FCSTD DOCUMENT  (FreeCAD 1.0R39109 (Git))
Label: 10_drawer_96mm_assembly
License: All rights reserved
LicenseURL: http://en.wikipedia.org/wiki/All_rights_reserved
objects: App::FeaturePython×17, App::Link×6, Assembly::JointGroup×1, Assembly::AssemblyObject×1
EXTERNAL_REF file=60_drawer_all_bottom.FCStd obj=Body
EXTERNAL_REF file=15_drawer_96mm_long.FCStd obj=Body
EXTERNAL_REF file=16_drawer_96mm_short.FCStd obj=Body
EXTERNAL_REF file=17_drawer_96mm_front.FCStd obj=Body

FEATURE [App::Link] Body
  LinkedObject = -> <external 60_drawer_all_bottom.FCStd>#Body
FEATURE [App::FeaturePython] GroundedJoint  # Assembly grounded joint (typed FeaturePython)
  ObjectToGround = -> Body
FEATURE [App::Link] Body001
  LinkPlacement = pos=(-0.0692255,177.5,34.4999) rot=(0.999999,-0.001116,0.001116;1.5708rad)
  LinkedObject = -> <external 15_drawer_96mm_long.FCStd>#Body
  Placement = pos=(-0.0692255,177.5,34.4999) rot=(0.999999,-0.001116,0.001116;1.5708rad)
FEATURE [App::Link] Body002
  LinkPlacement = pos=(2.3e-15,-177.5,34) rot=(0,0.707107,0.707107;3.14159rad)
  LinkedObject = -> <external 15_drawer_96mm_long.FCStd>#Body
  Placement = pos=(2.3e-15,-177.5,34) rot=(0,0.707107,0.707107;3.14159rad)
FEATURE [App::Link] Body003
  LinkPlacement = pos=(-231.5,-4.06e-14,34) rot=(0.57735,0.57735,0.57735;2.0944rad)
  LinkedObject = -> <external 16_drawer_96mm_short.FCStd>#Body
  Placement = pos=(-231.5,-4.06e-14,34) rot=(0.57735,0.57735,0.57735;2.0944rad)
FEATURE [App::Link] Body004
  LinkPlacement = pos=(231.5,-6.4e-15,34) rot=(0.57735,-0.57735,-0.57735;2.0944rad)
  LinkedObject = -> <external 16_drawer_96mm_short.FCStd>#Body
  Placement = pos=(231.5,-6.4e-15,34) rot=(0.57735,-0.57735,-0.57735;2.0944rad)
FEATURE [App::FeaturePython] Joint  label="Back1"  # Assembly joint (typed FeaturePython)
  Activated = true
  AngleMax = 0
  AngleMin = 0
  Detach1 = false
  Detach2 = false
  Distance = 0
  Distance2 = 0
  EnableAngleMax = false
  EnableAngleMin = false
  EnableLengthMax = false
  EnableLengthMin = false
  JointType = 5 (Distance)
  LengthMax = 0
  LengthMin = 0
  Placement1 = pos=(-2.3e-15,168.5,3.25) rot=(-1,0,0;1.5708rad)
  Placement2 = pos=(6.54e-14,-30.75,9) rot=(0.707107,0.707107,0;3.14159rad)
  Reference1 = -> Assembly [Body.Face1,Body.Face1]
  Reference2 = -> Assembly [Body001.Face7,Body001.Face7]
FEATURE [App::FeaturePython] Joint001  label="Back2"  # Assembly joint (typed FeaturePython)
  Activated = true
  AngleMax = 0
  AngleMin = 0
  Detach1 = false
  Detach2 = false
  Distance = 0.5
  Distance2 = 0
  EnableAngleMax = false
  EnableAngleMin = false
  EnableLengthMax = false
  EnableLengthMin = false
  JointType = 5 (Distance)
  LengthMax = 0
  LengthMin = 0
  Placement1 = pos=(7.41e-14,-34,12) rot=(0.57735,0.57735,-0.57735;2.0944rad)
  Placement2 = pos=(-2e-16,4.1e-15,0) rot=(0,0,1;0rad)
  Reference1 = -> Assembly [Body001.Face8,Body001.Vertex9]
  Reference2 = -> Assembly [Body.Face5,Body.Vertex1]
FEATURE [App::FeaturePython] Joint002  label="Back3"  # Assembly joint (typed FeaturePython)
  Activated = true
  AngleMax = 0
  AngleMin = 0
  Detach1 = false
  Detach2 = false
  Distance = 6
  Distance2 = 0
  EnableAngleMax = false
  EnableAngleMin = false
  EnableLengthMax = false
  EnableLengthMin = false
  JointType = 5 (Distance)
  LengthMax = 0
  LengthMin = 0
  Placement1 = pos=(-216.5,1.03295,7.34884) rot=(-0.57735,-0.57735,0.57735;2.0944rad)
  Placement2 = pos=(-222.5,-5.2e-15,3.25) rot=(-0.57735,-0.57735,0.57735;2.0944rad)
  Reference1 = -> Assembly [Body001.Face2,Body001.Face2]
  Reference2 = -> Assembly [Body.Face4,Body.Face4]
FEATURE [App::FeaturePython] Joint003  label="Left1"  # Assembly joint (typed FeaturePython)
  Activated = true
  AngleMax = 0
  AngleMin = 0
  Detach1 = false
  Detach2 = false
  Distance = 0
  Distance2 = 0
  EnableAngleMax = false
  EnableAngleMin = false
  EnableLengthMax = false
  EnableLengthMin = false
  JointType = 5 (Distance)
  LengthMax = 0
  LengthMin = 0
  Placement1 = pos=(-2e-16,4.1e-15,6.5) rot=(0,0,1;0rad)
  Placement2 = pos=(2.8e-15,-27.5,12) rot=(-0.57735,-0.57735,-0.57735;2.0944rad)
  Reference1 = -> Assembly [Body.Face6,Body.Face6]
  Reference2 = -> Assembly [Body003.Face6,Body003.Face6]
FEATURE [App::FeaturePython] Joint004  label="Left2"  # Assembly joint (typed FeaturePython)
  Activated = true
  AngleMax = 0
  AngleMin = 0
  Detach1 = false
  Detach2 = false
  Distance = 0
  Distance2 = 0
  EnableAngleMax = false
  EnableAngleMin = false
  EnableLengthMax = false
  EnableLengthMin = false
  JointType = 5 (Distance)
  LengthMax = 0
  LengthMin = 0
  Placement1 = pos=(9.3e-15,-30.75,9) rot=(-0.707107,-0.707107,0;3.14159rad)
  Placement2 = pos=(-222.5,-5.2e-15,3.25) rot=(-0.57735,-0.57735,0.57735;2.0944rad)
  Reference1 = -> Assembly [Body003.Face7,Body003.Face7]
  Reference2 = -> Assembly [Body.Face4,Body.Face4]
FEATURE [App::FeaturePython] Joint005  label="Left3"  # Assembly joint (typed FeaturePython)
  Activated = true
  AngleMax = 0
  AngleMin = 0
  Detach1 = false
  Detach2 = false
  Distance = 9
  Distance2 = 0
  EnableAngleMax = false
  EnableAngleMin = false
  EnableLengthMax = false
  EnableLengthMin = false
  JointType = 5 (Distance)
  LengthMax = 0
  LengthMin = 0
  Placement1 = pos=(2.3e-15,-168.5,3.25) rot=(0,-0.707107,0.707107;3.14159rad)
  Placement2 = pos=(-177.5,1.03295,7.34884) rot=(-0.57735,-0.57735,0.57735;2.0944rad)
  Reference1 = -> Assembly [Body.Face3,Body.Face3]
  Reference2 = -> Assembly [Body003.Face2,Body003.Face2]
FEATURE [App::FeaturePython] Joint006  label="Distance"  # Assembly joint (typed FeaturePython)
  Activated = true
  AngleMax = 0
  AngleMin = 0
  Detach1 = false
  Detach2 = false
  Distance = 0
  Distance2 = 0
  EnableAngleMax = false
  EnableAngleMin = false
  EnableLengthMax = false
  EnableLengthMin = false
  JointType = 5 (Distance)
  LengthMax = 0
  LengthMin = 0
  Placement1 = pos=(6.6e-14,-27.5,12) rot=(-0.57735,-0.57735,-0.57735;2.0944rad)
  Placement2 = pos=(-2e-16,4.1e-15,6.5) rot=(0,0,1;0rad)
  Reference1 = -> Assembly [Body002.Face6,Body002.Face6]
  Reference2 = -> Assembly [Body.Face6,Body.Face6]
FEATURE [App::FeaturePython] Joint007  label="Distance001"  # Assembly joint (typed FeaturePython)
  Activated = true
  AngleMax = 0
  AngleMin = 0
  Detach1 = false
  Detach2 = false
  Distance = 0
  Distance2 = 0
  EnableAngleMax = false
  EnableAngleMin = false
  EnableLengthMax = false
  EnableLengthMin = false
  JointType = 5 (Distance)
  LengthMax = 0
  LengthMin = 0
  Placement1 = pos=(2.3e-15,-168.5,3.25) rot=(0,-0.707107,0.707107;3.14159rad)
  Placement2 = pos=(6.88e-14,-30.75,9) rot=(0.707107,0.707107,0;3.14159rad)
  Reference1 = -> Assembly [Body.Face3,Body.Face3]
  Reference2 = -> Assembly [Body002.Face7,Body002.Vertex8]
FEATURE [App::FeaturePython] Joint008  label="Distance002"  # Assembly joint (typed FeaturePython)
  Activated = true
  AngleMax = 0
  AngleMin = 0
  Detach1 = false
  Detach2 = false
  Distance = -6
  Distance2 = 0
  EnableAngleMax = false
  EnableAngleMin = false
  EnableLengthMax = false
  EnableLengthMin = false
  JointType = 5 (Distance)
  LengthMax = 0
  LengthMin = 0
  Placement1 = pos=(222.5,5.2e-15,3.25) rot=(0.57735,-0.57735,0.57735;4.18879rad)
  Placement2 = pos=(-216.5,1.03295,7.34884) rot=(-0.57735,-0.57735,0.57735;2.0944rad)
  Reference1 = -> Assembly [Body.Face2,Body.Face2]
  Reference2 = -> Assembly [Body002.Face2,Body002.Face2]
FEATURE [App::FeaturePython] Joint009  label="Rigth1"  # Assembly joint (typed FeaturePython)
  Activated = true
  AngleMax = 0
  AngleMin = 0
  Detach1 = false
  Detach2 = false
  Distance = 0
  Distance2 = 0
  EnableAngleMax = false
  EnableAngleMin = false
  EnableLengthMax = false
  EnableLengthMin = false
  JointType = 5 (Distance)
  LengthMax = 0
  LengthMin = 0
  Placement1 = pos=(-1.05e-14,-27.5,12) rot=(0.57735,0.57735,0.57735;4.18879rad)
  Placement2 = pos=(-2e-16,4.1e-15,6.5) rot=(0,0,1;0rad)
  Reference1 = -> Assembly [Body004.Face6,Body004.Face6]
  Reference2 = -> Assembly [Body.Face6,Body.Face6]
FEATURE [App::FeaturePython] Joint010  label="Rigth2"  # Assembly joint (typed FeaturePython)
  Activated = true
  AngleMax = 0
  AngleMin = 0
  Detach1 = false
  Detach2 = false
  Distance = 0
  Distance2 = 0
  EnableAngleMax = false
  EnableAngleMin = false
  EnableLengthMax = false
  EnableLengthMin = false
  JointType = 5 (Distance)
  LengthMax = 0
  LengthMin = 0
  Placement1 = pos=(-4.9e-15,-30.75,9) rot=(0.707107,0.707107,0;3.14159rad)
  Placement2 = pos=(222.5,5.2e-15,3.25) rot=(0.57735,-0.57735,0.57735;4.18879rad)
  Reference1 = -> Assembly [Body004.Face7,Body004.Vertex8]
  Reference2 = -> Assembly [Body.Face2,Body.Vertex5]
FEATURE [App::FeaturePython] Joint011  label="Right3"  # Assembly joint (typed FeaturePython)
  Activated = true
  AngleMax = 0
  AngleMin = 0
  Detach1 = false
  Detach2 = false
  Distance = 9
  Distance2 = 0
  EnableAngleMax = false
  EnableAngleMin = false
  EnableLengthMax = false
  EnableLengthMin = false
  JointType = 5 (Distance)
  LengthMax = 0
  LengthMin = 0
  Placement1 = pos=(2.3e-15,-168.5,3.25) rot=(0,-0.707107,0.707107;3.14159rad)
  Placement2 = pos=(177.5,1.03295,7.34884) rot=(0.57735,-0.57735,0.57735;4.18879rad)
  Reference1 = -> Assembly [Body.Face3,Body.Vertex5]
  Reference2 = -> Assembly [Body004.Face3,Body004.Face3]
FEATURE [App::Link] Body005
  LinkPlacement = pos=(2.5e-15,-177.5,33.5) rot=(0,-0.707107,0.707107;3.14159rad)
  LinkedObject = -> <external 17_drawer_96mm_front.FCStd>#Body
  Placement = pos=(2.5e-15,-177.5,33.5) rot=(0,-0.707107,0.707107;3.14159rad)
FEATURE [App::FeaturePython] Joint012  label="Front1"  # Assembly joint (typed FeaturePython)
  Activated = true
  AngleMax = 0
  AngleMin = 0
  Detach1 = false
  Detach2 = false
  Distance = 0
  Distance2 = 0
  EnableAngleMax = false
  EnableAngleMin = false
  EnableLengthMax = false
  EnableLengthMin = false
  JointType = 5 (Distance)
  LengthMax = 0
  LengthMin = 0
  Placement1 = pos=(2e-15,0,0) rot=(0,0,1;0rad)
  Placement2 = pos=(3e-15,0,0) rot=(0,0,1;0rad)
  Reference1 = -> Assembly [Body005.Face5,Body005.Face5]
  Reference2 = -> Assembly [Body002.Face4,Body002.Face4]
FEATURE [App::FeaturePython] Joint013  label="Front2"  # Assembly joint (typed FeaturePython)
  Activated = true
  AngleMax = 0
  AngleMin = 0
  Detach1 = false
  Detach2 = false
  Distance = 6
  Distance2 = 0
  EnableAngleMax = false
  EnableAngleMin = false
  EnableLengthMax = false
  EnableLengthMin = false
  JointType = 5 (Distance)
  LengthMax = 0
  LengthMin = 0
  Placement1 = pos=(8.3e-15,40,7.5) rot=(-1,0,0;1.5708rad)
  Placement2 = pos=(7.1e-15,-46.5,7.5) rot=(0,0.707107,-0.707107;3.14159rad)
  Reference1 = -> Assembly [Body002.Face1,Body002.Face1]
  Reference2 = -> Assembly [Body005.Face3,Body005.Face3]
FEATURE [App::FeaturePython] Joint014  label="Distance003"  # Assembly joint (typed FeaturePython)
  Activated = true
  AngleMax = 0
  AngleMin = 0
  Detach1 = false
  Detach2 = false
  Distance = -29
  Distance2 = 0
  EnableAngleMax = false
  EnableAngleMin = false
  EnableLengthMax = false
  EnableLengthMin = false
  JointType = 5 (Distance)
  LengthMax = 0
  LengthMin = 0
  Placement1 = pos=(1.4e-15,0,0) rot=(0,0,1;0rad)
  Placement2 = pos=(260.5,0,7.5) rot=(-0.57735,0.57735,-0.57735;2.0944rad)
  Reference1 = -> Assembly [Body003.Face4,Body003.Face4]
  Reference2 = -> Assembly [Body005.Face2,Body005.Face2]
FEATURE [App::FeaturePython] Joint015  label="Distance004"  # Assembly joint (typed FeaturePython)
  Activated = true
  AngleMax = 0
  AngleMin = 0
  Detach1 = false
  Detach2 = false
  Distance = 0
  Distance2 = 0
  EnableAngleMax = false
  EnableAngleMin = false
  EnableLengthMax = false
  EnableLengthMin = false
  JointType = 5 (Distance)
  LengthMax = 0
  LengthMin = 0
  Placement1 = pos=(1.72e-14,40,7.5) rot=(-1,0,0;1.5708rad)
  Placement2 = pos=(6.2e-15,40,7.5) rot=(-1,0,0;1.5708rad)
  Reference1 = -> Assembly [Body001.Face1,Body001.Vertex2]
  Reference2 = -> Assembly [Body003.Face1,Body003.Vertex4]
FEATURE [Assembly::JointGroup] Joints
  Group = -> [GroundedJoint,Joint,Joint001,Joint002,Joint003,Joint004,Joint005,Joint006,Joint007,Joint008,Joint009,Joint010,Joint011,Joint012,Joint013,Joint014,Joint015]
FEATURE [Assembly::AssemblyObject] Assembly
  Group = -> [Joints,Body,GroundedJoint,Body001,Body002,Body003,Body004,Joint,Joint001,Joint002,Joint003,Joint004,Joint005,Joint006,Joint007,Joint008,Joint009,Joint010,Joint011,Body005,Joint012,Joint013,Joint014,Joint015]
  Origin = -> Origin
  Type = Assembly

RESOLVED EXTERNAL PARTS (link-assembly join: the EXTERNAL_REF files above that resolve inside this repo's crawl, each included once):
---- part 15_drawer_96mm_long.FCStd = doc fcstd_027bf1619f1c ----
FCSTD DOCUMENT  (FreeCAD 1.0R39109 (Git))
Label: 15_drawer_96mm_long
License: All rights reserved
LicenseURL: http://en.wikipedia.org/wiki/All_rights_reserved
objects: Sketcher::SketchObject×2, Spreadsheet::Sheet×1, PartDesign::Pad×1, PartDesign::Pocket×1, PartDesign::Body×1
note: 11 computed .brp shape members not serialized (recipe doc carries the construction recipe); baked Part::Feature solids carry a one-line shape summary decoded from their .brp

FEATURE [Spreadsheet::Sheet] Spreadsheet
  cells = A2='length; B2(length)=433; D2='space: 2mm; A3='width; B3(width)=80; D3='space: 2mm; A4='height; B4(height)=15; A6='Groove Depth; B6(grooveDepth)=6; A7='Groove Distance; B7(grooveDistance)=6; A8='Groove Width; B8(grooveWidth)=6.5
FEATURE [Sketcher::SketchObject] Sketch
  ArcFitTolerance = 0
  AttachmentSupport = -> [XY_Plane]
  FullyConstrained = true
  MakeInternals = false
  MapMode = 5
  expr: Constraints[11] = Spreadsheet.length
  expr: Constraints[12] = Spreadsheet.width
  sketch-geometry (5):
    g0: LineSegment StartX=-216.5 StartY=40 StartZ=0 EndX=216.5 EndY=40 EndZ=0
    g1: LineSegment StartX=216.5 StartY=40 StartZ=0 EndX=216.5 EndY=-40 EndZ=0
    g2: LineSegment StartX=216.5 StartY=-40 StartZ=0 EndX=-216.5 EndY=-40 EndZ=0
    g3: LineSegment StartX=-216.5 StartY=-40 StartZ=0 EndX=-216.5 EndY=40 EndZ=0
    g4: LineSegment [constr] StartX=-216.5 StartY=40 StartZ=0 EndX=216.5 EndY=-40 EndZ=0
  constraints (13):
    c: Coincident(g0,g1)
    c: Coincident(g1,g2)
    c: Coincident(g2,g3)
    c: Coincident(g3,g0)
    c: Horizontal(g0)
    c: Horizontal(g2)
    c: Vertical(g1)
    c: Vertical(g3)
    c: Coincident(g4,g1)
    c: Coincident(g0,g4)
    c: Symmetric(g0,g1,g-1)
    c: Distance(g0,g0) = 433
    c: Distance(g0,g2) = 80
FEATURE [PartDesign::Pad] Pad
  Direction = (0,0,1)
  Length = 15
  Length2 = 10
  Profile = -> Sketch
  ReferenceAxis = -> Sketch [N_Axis]
  Suppressed = false
  Type = 0
  expr: Length = Spreadsheet.height
FEATURE [Sketcher::SketchObject] Sketch001
  ArcFitTolerance = 1e-06
  AttachmentSupport = -> [YZ_Plane]
  ExternalGeometry = -> [Pad]
  FullyConstrained = true
  MakeInternals = false
  MapMode = 5
  Placement = pos=(0,0,0) rot=(0.57735,0.57735,0.57735;2.0944rad)
  sketch-geometry (4):
    g0: LineSegment StartX=-34 StartY=15 StartZ=0 EndX=-34 EndY=9 EndZ=0
    g1: LineSegment StartX=-34 StartY=9 StartZ=0 EndX=-27.5 EndY=9 EndZ=0
    g2: LineSegment StartX=-27.5 StartY=9 StartZ=0 EndX=-27.5 EndY=15 EndZ=0
    g3: LineSegment StartX=-27.5 StartY=15 StartZ=0 EndX=-34 EndY=15 EndZ=0
  constraints (12):
    c: Coincident(g0,g1)
    c: Coincident(g1,g2)
    c: Coincident(g2,g3)
    c: Coincident(g3,g0)
    c: Vertical(g0)
    c: Vertical(g2)
    c: Horizontal(g1)
    c: Horizontal(g3)
    c: PointOnObject(g0,g-3)
    c: DistanceX(g3,g3) = 6.5
    c: Distance(g-4,g0) = 6
    c: DistanceY(g2,g2) = 6
FEATURE [PartDesign::Pocket] Pocket
  BaseFeature = -> Pad
  Direction = (-1,0,0)
  Length = 5
  Length2 = 5
  Midplane = true
  Profile = -> Sketch001
  ReferenceAxis = -> Sketch001 [N_Axis]
  Suppressed = false
  Type = 1
FEATURE [PartDesign::Body] Body
  AllowCompound = false
  Group = -> [Sketch,Pad,Sketch001,Pocket]
  Origin = -> Origin
  Tip = -> Pocket
---- part 16_drawer_96mm_short.FCStd = doc fcstd_3ad6f7a57b24 ----
FCSTD DOCUMENT  (FreeCAD 1.0R39109 (Git))
Label: 16_drawer_96mm_short
License: All rights reserved
LicenseURL: http://en.wikipedia.org/wiki/All_rights_reserved
objects: Sketcher::SketchObject×2, Spreadsheet::Sheet×1, PartDesign::Pad×1, PartDesign::Pocket×1, PartDesign::Body×1
note: 11 computed .brp shape members not serialized (recipe doc carries the construction recipe); baked Part::Feature solids carry a one-line shape summary decoded from their .brp

FEATURE [Spreadsheet::Sheet] Spreadsheet
  cells = A2='length; B2(length)=355; D2='space: 1mm; A3='width; B3(width)=80; D3='space: 1mm; A4='height; B4(height)=15; A6='Groove Depth; B6(grooveDepth)=6; A7='Groove Distance; B7(grooveDistance)=6; A8='Groove Width; B8(grooveWidth)=6.5
FEATURE [Sketcher::SketchObject] Sketch
  ArcFitTolerance = 0
  AttachmentSupport = -> [XY_Plane]
  FullyConstrained = true
  MakeInternals = false
  MapMode = 5
  expr: Constraints[11] = Spreadsheet.length
  expr: Constraints[12] = Spreadsheet.width
  sketch-geometry (5):
    g0: LineSegment StartX=-177.5 StartY=40 StartZ=0 EndX=177.5 EndY=40 EndZ=0
    g1: LineSegment StartX=177.5 StartY=40 StartZ=0 EndX=177.5 EndY=-40 EndZ=0
    g2: LineSegment StartX=177.5 StartY=-40 StartZ=0 EndX=-177.5 EndY=-40 EndZ=0
    g3: LineSegment StartX=-177.5 StartY=-40 StartZ=0 EndX=-177.5 EndY=40 EndZ=0
    g4: LineSegment [constr] StartX=-177.5 StartY=40 StartZ=0 EndX=177.5 EndY=-40 EndZ=0
  constraints (13):
    c: Coincident(g0,g1)
    c: Coincident(g1,g2)
    c: Coincident(g2,g3)
    c: Coincident(g3,g0)
    c: Horizontal(g0)
    c: Horizontal(g2)
    c: Vertical(g1)
    c: Vertical(g3)
    c: Coincident(g4,g1)
    c: Coincident(g0,g4)
    c: Symmetric(g0,g1,g-1)
    c: Distance(g0,g0) = 355
    c: Distance(g0,g2) = 80
FEATURE [PartDesign::Pad] Pad
  Direction = (0,0,1)
  Length = 15
  Length2 = 10
  Profile = -> Sketch
  ReferenceAxis = -> Sketch [N_Axis]
  Suppressed = false
  Type = 0
  expr: Length = Spreadsheet.height
FEATURE [Sketcher::SketchObject] Sketch001
  ArcFitTolerance = 1e-06
  AttachmentSupport = -> [YZ_Plane]
  ExternalGeometry = -> [Pad]
  FullyConstrained = true
  MakeInternals = false
  MapMode = 5
  Placement = pos=(0,0,0) rot=(0.57735,0.57735,0.57735;2.0944rad)
  sketch-geometry (4):
    g0: LineSegment StartX=-34 StartY=15 StartZ=0 EndX=-34 EndY=9 EndZ=0
    g1: LineSegment StartX=-34 StartY=9 StartZ=0 EndX=-27.5 EndY=9 EndZ=0
    g2: LineSegment StartX=-27.5 StartY=9 StartZ=0 EndX=-27.5 EndY=15 EndZ=0
    g3: LineSegment StartX=-27.5 StartY=15 StartZ=0 EndX=-34 EndY=15 EndZ=0
  constraints (12):
    c: Coincident(g0,g1)
    c: Coincident(g1,g2)
    c: Coincident(g2,g3)
    c: Coincident(g3,g0)
    c: Vertical(g0)
    c: Vertical(g2)
    c: Horizontal(g1)
    c: Horizontal(g3)
    c: PointOnObject(g0,g-4)
    c: DistanceX(g3,g3) = 6.5
    c: Distance(g0,g0) = 6
    c: Distance(g-4,g0) = 6
FEATURE [PartDesign::Pocket] Pocket
  BaseFeature = -> Pad
  Direction = (-1,0,0)
  Length = 5
  Length2 = 5
  Midplane = true
  Profile = -> Sketch001
  ReferenceAxis = -> Sketch001 [N_Axis]
  Suppressed = false
  Type = 1
FEATURE [PartDesign::Body] Body
  AllowCompound = false
  Group = -> [Sketch,Pad,Sketch001,Pocket]
  Origin = -> Origin
  Tip = -> Pocket
---- part 17_drawer_96mm_front.FCStd = doc fcstd_0fb94227f05c ----
FCSTD DOCUMENT  (FreeCAD 1.0R39109 (Git))
Label: 17_drawer_96mm_front
License: All rights reserved
LicenseURL: http://en.wikipedia.org/wiki/All_rights_reserved
objects: Spreadsheet::Sheet×1, Sketcher::SketchObject×1, PartDesign::Pad×1, PartDesign::Body×1
note: 6 computed .brp shape members not serialized (recipe doc carries the construction recipe); baked Part::Feature solids carry a one-line shape summary decoded from their .brp

FEATURE [Spreadsheet::Sheet] Spreadsheet
  cells = A2='length; B2(length)=521; A3='width; B3(width)=93; A4='height; B4(height)=15; D9=433; D10==D9 + 30; E10==B2 - D10; E11==E10 / 2
FEATURE [Sketcher::SketchObject] Sketch
  ArcFitTolerance = 0
  AttachmentSupport = -> [XY_Plane]
  FullyConstrained = true
  MakeInternals = false
  MapMode = 5
  expr: Constraints[11] = Spreadsheet.length
  expr: Constraints[12] = Spreadsheet.width
  sketch-geometry (5):
    g0: LineSegment StartX=-260.5 StartY=46.5 StartZ=0 EndX=260.5 EndY=46.5 EndZ=0
    g1: LineSegment StartX=260.5 StartY=46.5 StartZ=0 EndX=260.5 EndY=-46.5 EndZ=0
    g2: LineSegment StartX=260.5 StartY=-46.5 StartZ=0 EndX=-260.5 EndY=-46.5 EndZ=0
    g3: LineSegment StartX=-260.5 StartY=-46.5 StartZ=0 EndX=-260.5 EndY=46.5 EndZ=0
    g4: LineSegment [constr] StartX=-260.5 StartY=46.5 StartZ=0 EndX=260.5 EndY=-46.5 EndZ=0
  constraints (13):
    c: Coincident(g0,g1)
    c: Coincident(g1,g2)
    c: Coincident(g2,g3)
    c: Coincident(g3,g0)
    c: Horizontal(g0)
    c: Horizontal(g2)
    c: Vertical(g1)
    c: Vertical(g3)
    c: Coincident(g4,g1)
    c: Coincident(g0,g4)
    c: Symmetric(g0,g1,g-1)
    c: Distance(g0,g0) = 521
    c: Distance(g0,g2) = 93
FEATURE [PartDesign::Pad] Pad
  Direction = (0,0,1)
  Length = 15
  Length2 = 10
  Profile = -> Sketch
  ReferenceAxis = -> Sketch [N_Axis]
  Suppressed = false
  Type = 0
  expr: Length = Spreadsheet.height
FEATURE [PartDesign::Body] Body
  AllowCompound = false
  Group = -> [Sketch,Pad]
  Origin = -> Origin
  Tip = -> Pad
---- part 60_drawer_all_bottom.FCStd = doc fcstd_0f60ed07a972 ----
FCSTD DOCUMENT  (FreeCAD 1.0R39109 (Git))
Label: 60_drawer_all_bottom
License: All rights reserved
LicenseURL: http://en.wikipedia.org/wiki/All_rights_reserved
objects: Spreadsheet::Sheet×1, Sketcher::SketchObject×1, PartDesign::Pad×1, PartDesign::Body×1
note: 6 computed .brp shape members not serialized (recipe doc carries the construction recipe); baked Part::Feature solids carry a one-line shape summary decoded from their .brp

FEATURE [Spreadsheet::Sheet] Spreadsheet
  cells = A2='length; B2(length)=445; A3='width; B3(width)=337; A4='height; B4(height)=6.5
FEATURE [Sketcher::SketchObject] Sketch
  ArcFitTolerance = 0
  AttachmentSupport = -> [XY_Plane]
  FullyConstrained = true
  MakeInternals = false
  MapMode = 5
  expr: Constraints[11] = Spreadsheet.length
  expr: Constraints[12] = Spreadsheet.width
  sketch-geometry (5):
    g0: LineSegment StartX=-222.5 StartY=168.5 StartZ=0 EndX=222.5 EndY=168.5 EndZ=0
    g1: LineSegment StartX=222.5 StartY=168.5 StartZ=0 EndX=222.5 EndY=-168.5 EndZ=0
    g2: LineSegment StartX=222.5 StartY=-168.5 StartZ=0 EndX=-222.5 EndY=-168.5 EndZ=0
    g3: LineSegment StartX=-222.5 StartY=-168.5 StartZ=0 EndX=-222.5 EndY=168.5 EndZ=0
    g4: LineSegment [constr] StartX=-222.5 StartY=168.5 StartZ=0 EndX=222.5 EndY=-168.5 EndZ=0
  constraints (13):
    c: Coincident(g0,g1)
    c: Coincident(g1,g2)
    c: Coincident(g2,g3)
    c: Coincident(g3,g0)
    c: Horizontal(g0)
    c: Horizontal(g2)
    c: Vertical(g1)
    c: Vertical(g3)
    c: Coincident(g4,g1)
    c: Coincident(g0,g4)
    c: Symmetric(g0,g1,g-1)
    c: Distance(g0,g0) = 445
    c: Distance(g0,g2) = 337
FEATURE [PartDesign::Pad] Pad
  Direction = (0,0,1)
  Length = 6.5
  Length2 = 10
  Profile = -> Sketch
  ReferenceAxis = -> Sketch [N_Axis]
  Suppressed = false
  Type = 0
  expr: Length = Spreadsheet.height
FEATURE [PartDesign::Body] Body
  AllowCompound = false
  Group = -> [Sketch,Pad]
  Origin = -> Origin
  Tip = -> Pad
